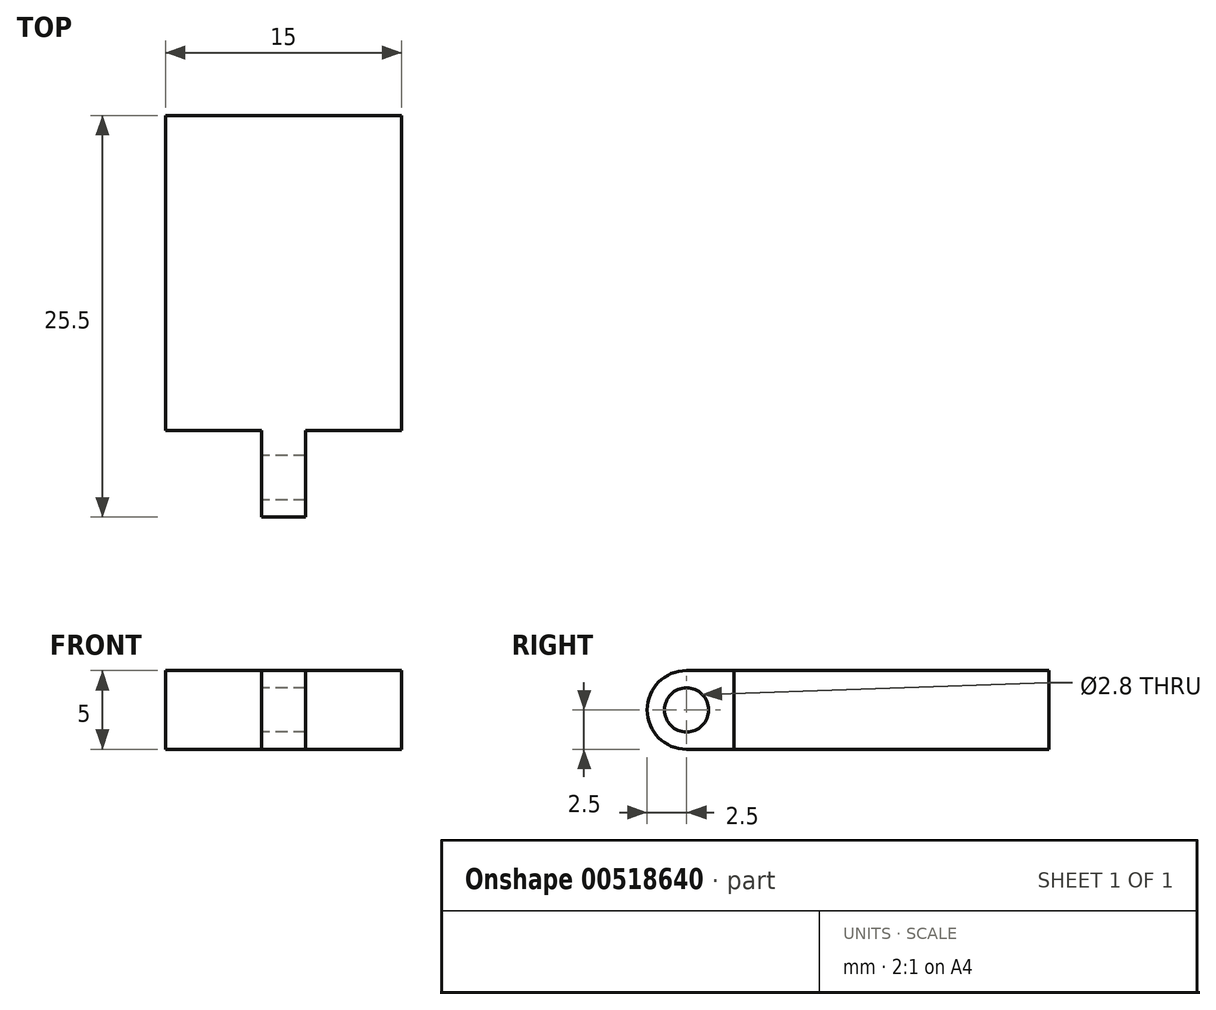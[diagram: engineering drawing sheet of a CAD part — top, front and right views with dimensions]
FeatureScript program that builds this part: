
annotation { "Feature Type Name" : "Feature", "Feature Type Description" : "" }
export const myFeature = defineFeature(function(context is Context, id is Id, definition is map)
    precondition{}
    {
        {
            var Q0;
            Q0=qCreatedBy(makeId("Top.planeOp"),FACE);
            var sketch = newSketch(context, id + "F0", { "sketchPlane" : qUnion([Q0])});
            skLineSegment(sketch, "E0.bottom", {"start": v(-7.5, 10) * mm, "end": v(7.5, 10) * mm});
            skLineSegment(sketch, "E0.top", {"start": v(-7.5, -10) * mm, "end": v(7.5, -10) * mm});
            skLineSegment(sketch, "E0.left", {"start": v(-7.5, 10) * mm, "end": v(-7.5, -10) * mm});
            skLineSegment(sketch, "E0.right", {"start": v(7.5, 10) * mm, "end": v(7.5, -10) * mm});
            skSolve(sketch);
        }
        {
            var Q0;
            Q0=makeQuery(id+"F0.imprint","IMPRINT",FACE,{"disambiguationData":[TD([[makeQuery(id+"F0.imprint","IMPRINT",EDGE,{"derivedFrom":sQuery(id+"F0.wireOp",EDGE,"E0.bottom")}),-1.0]])]});
            extrude(context, id + "F1", {"entities" : qUnion([Q0]), "depth" : 5 * mm, "offsetDistance" : 25 * mm});
        }
        {
            var Q0;
            Q0=makeQuery(id+"F1.opExtrude","SWEPT_FACE",FACE,{"disambiguationData":[OSD([sQuery(id+"F0.wireOp",EDGE,"E0.top")])]});
            var sketch = newSketch(context, id + "F2", { "sketchPlane" : qUnion([Q0])});
            skLineSegment(sketch, "E1.bottom", {"start": v(-1.4, 5) * mm, "end": v(1.4, 5) * mm});
            skLineSegment(sketch, "E1.top", {"start": v(-1.4, 0) * mm, "end": v(1.4, 0) * mm});
            skLineSegment(sketch, "E1.left", {"start": v(-1.4, 5) * mm, "end": v(-1.4, 0) * mm});
            skLineSegment(sketch, "E1.right", {"start": v(1.4, 5) * mm, "end": v(1.4, 0) * mm});
            skSolve(sketch);
        }
        {
            var Q0;
            Q0=makeQuery(id+"F2.imprint","IMPRINT",FACE,{"disambiguationData":[TD([[makeQuery(id+"F2.imprint","IMPRINT",EDGE,{"derivedFrom":sQuery(id+"F2.wireOp",EDGE,"E1.bottom")}),-1.0]])]});
            extrude(context, id + "F3", {"entities" : qUnion([Q0]), "operationType" : NewBodyOperationType.ADD, "depth" : 3 * mm, "offsetDistance" : 25 * mm});
        }
        {
            var Q0;
            Q0=makeQuery(id+"F3.opExtrude","CAP_FACE",FACE,{"disambiguationData":[OSD([sQuery(id+"F2.wireOp",EDGE,"E1.bottom"),sQuery(id+"F2.wireOp",EDGE,"E1.top"),sQuery(id+"F2.wireOp",EDGE,"E1.left"),sQuery(id+"F2.wireOp",EDGE,"E1.right")])],"isStart":false});
            var sketch = newSketch(context, id + "F4", { "sketchPlane" : qUnion([Q0])});
            skLineSegment(sketch, "E2", {"start": v(-1.4, 2.5) * mm, "end": v(1.4, 2.5) * mm});
            skSolve(sketch);
        }
        {
            var Q0;
            {var subQ0=sQuery(id+"F4.wireOp",EDGE,"E2");Q0=makeQuery(id+"F4.imprint","IMPRINT",FACE,{"disambiguationData":[TD([[makeQuery(id+"F4.imprint","IMPRINT",EDGE,{"derivedFrom":subQ0}),-1.0]])]});}
            var Q1;
            Q1=sQuery(id+"F4.wireOp",EDGE,"E2");
            revolve(context, id + "F5", {"operationType" : NewBodyOperationType.ADD, "entities" : qUnion([Q0]), "axis" : qUnion([Q1]), "revolveType" : RevolveType.FULL});
        }
        {
            var Q0;
            {var subQ0=sQuery(id+"F2.wireOp",EDGE,"E1.left");Q0=makeQuery(id+"F5.boolean.opBoolean","MERGE",FACE,{"derivedFrom":[makeQuery(id+"F3.opExtrude","SWEPT_FACE",FACE,{"disambiguationData":[OSD([subQ0])]}),makeQuery(id+"F5.opRevolve","SWEPT_FACE",FACE,{"disambiguationData":[OSD([subQ0])]})]});}
            var sketch = newSketch(context, id + "F6", { "sketchPlane" : qUnion([Q0])});
            skCircle(sketch, "E3", {"center": v(13, 2.5) * mm, "radius": 1.4 * mm});
            skSolve(sketch);
        }
        {
            var Q0;
            Q0=makeQuery(id+"F6.imprint","IMPRINT",FACE,{"disambiguationData":[TD([[makeQuery(id+"F6.imprint","IMPRINT",EDGE,{"derivedFrom":sQuery(id+"F6.wireOp",EDGE,"E3")}),1.0]])]});
            extrude(context, id + "F7", {"entities" : qUnion([Q0]), "operationType" : NewBodyOperationType.REMOVE, "oppositeDirection" : true, "depth" : 5 * mm, "offsetDistance" : 25 * mm});
        }
    });
